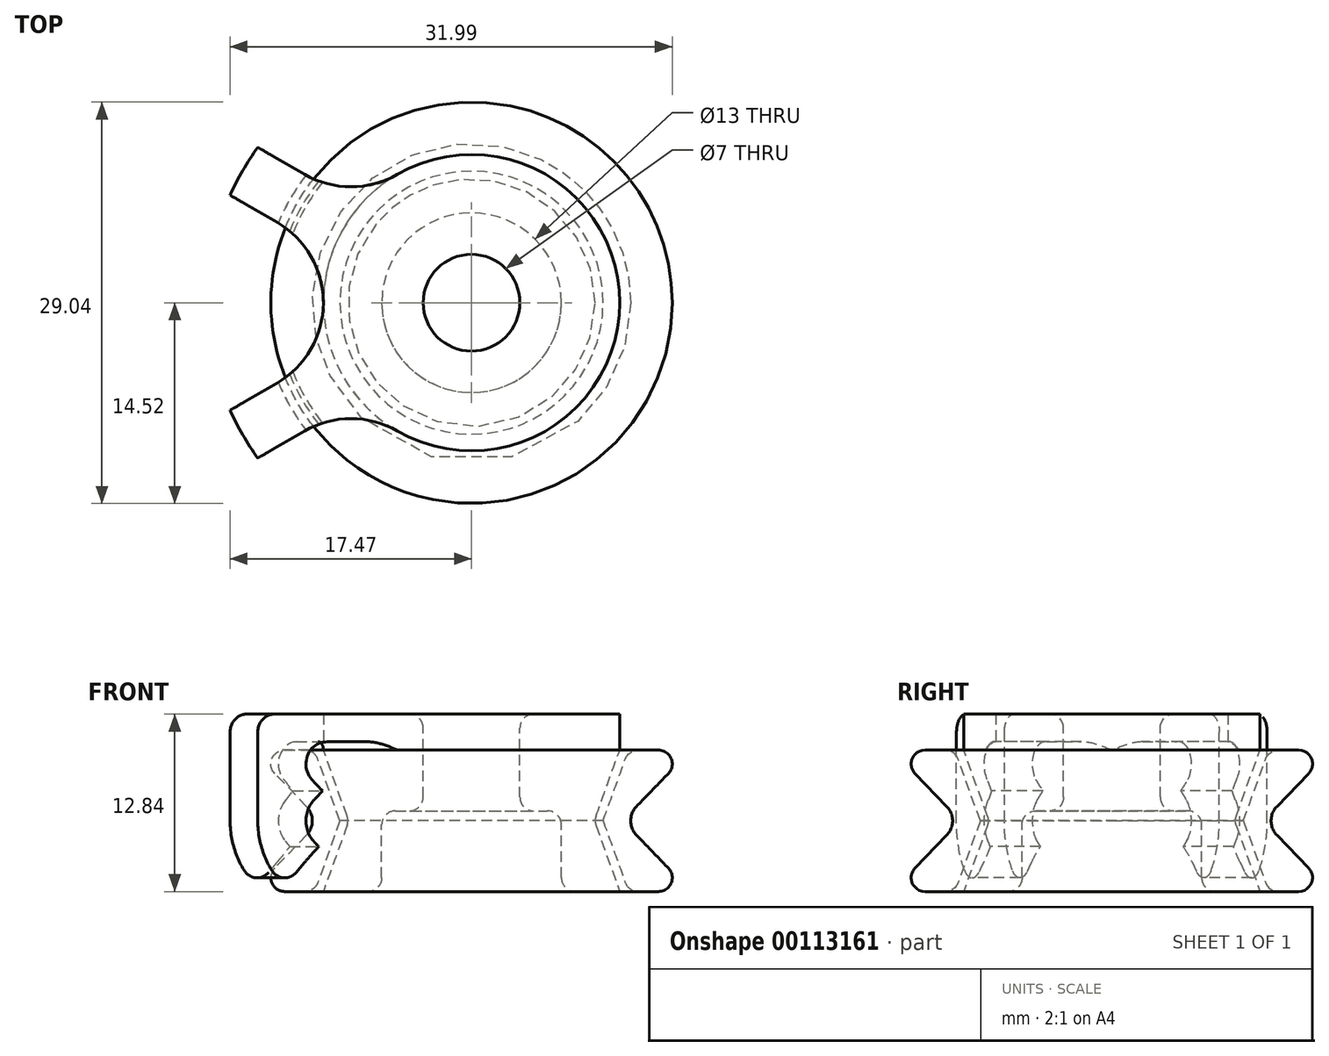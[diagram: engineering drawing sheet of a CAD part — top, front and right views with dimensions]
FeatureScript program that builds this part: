
annotation { "Feature Type Name" : "Feature", "Feature Type Description" : "" }
export const myFeature = defineFeature(function(context is Context, id is Id, definition is map)
    precondition{}
    {
        {
            assignVariable(context, id + "F0", {"name" : "WALL", "anyValue" : 4});
        }
        {
            assignVariable(context, id + "F1", {"name" : "ArmAngle", "anyValue" : 60});
        }
        {
            assignVariable(context, id + "F2", {"name" : "NumberArms", "anyValue" : 2});
        }
        {
            var Q0;
            Q0=qCreatedBy(makeId("Front.planeOp"),FACE);
            var sketch = newSketch(context, id + "F3", { "sketchPlane" : qUnion([Q0])});
            skLineSegment(sketch, "E0", {"start": v(0, 5.12) * mm, "end": v(0, -5.12) * mm});
            skLineSegment(sketch, "E1", {"start": v(-11.36, -5.12) * mm, "end": v(-13.52, -5.12) * mm});
            skLineSegment(sketch, "E2", {"start": v(-13.52, 5.12) * mm, "end": v(-11.36, 5.12) * mm});
            skCircle(sketch, "E3", {"center": v(-13.02, 0) * mm, "radius": 1.5 * mm, "construction": true});
            skLineSegment(sketch, "E4", {"start": v(-11.94, 1.04) * mm, "end": v(-14.24, 3.42) * mm});
            skLineSegment(sketch, "E5", {"start": v(-14.24, -3.42) * mm, "end": v(-11.94, -1.04) * mm});
            skArc(sketch, "E6", {"start": v(-11.94, -1.04) * mm, "mid": v(-11.52, 0) * mm, "end": v(-11.94, 1.04) * mm});
            skLineSegment(sketch, "E7", {"start": v(-11.36, 5.12) * mm, "end": v(-9.52, 0) * mm});
            skLineSegment(sketch, "E8", {"start": v(-9.52, 0) * mm, "end": v(-11.36, -5.12) * mm});
            skLineSegment(sketch, "E9", {"start": v(-10.72, 5.12) * mm, "end": v(-8.88, 0) * mm});
            skLineSegment(sketch, "E10", {"start": v(-8.88, 0) * mm, "end": v(-10.72, -5.12) * mm});
            skLineSegment(sketch, "E11", {"start": v(-10.72, 5.12) * mm, "end": v(-6.5, 5.12) * mm});
            skLineSegment(sketch, "E12", {"start": v(-6.5, 5.12) * mm, "end": v(-6.5, -5.12) * mm});
            skLineSegment(sketch, "E13", {"start": v(-6.5, -5.12) * mm, "end": v(-10.72, -5.12) * mm});
            skArc(sketch, "E14", {"start": v(-14.53, 1.46) * mm, "mid": v(-15.12, 0) * mm, "end": v(-14.53, -1.46) * mm});
            skLineSegment(sketch, "E15", {"start": v(-10.72, 5.12) * mm, "end": v(-10.72, 5.12) * mm});
            skLineSegment(sketch, "E16", {"start": v(-11.32, 5.72) * mm, "end": v(-13.52, 5.72) * mm});
            skLineSegment(sketch, "E17", {"start": v(-6.5, 5.12) * mm, "end": v(-6.5, 7.72) * mm});
            skLineSegment(sketch, "E18", {"start": v(-6.5, 7.72) * mm, "end": v(-19.12, 7.72) * mm});
            skLineSegment(sketch, "E19", {"start": v(-16.88, -4.72) * mm, "end": v(-14.13, -1.87) * mm});
            skLineSegment(sketch, "E20", {"start": v(-14.53, 1.46) * mm, "end": v(-13.85, 2.16) * mm});
            skLineSegment(sketch, "E21", {"start": v(-14.53, -1.46) * mm, "end": v(-14.13, -1.87) * mm});
            skPoint(sketch, "E22.visualSharp", {"position": v(-15.88, 5.12) * mm});
            skArc(sketch, "E22.filletArc", {"start": v(-13.52, 5.12) * mm, "mid": v(-14.44, 4.5) * mm, "end": v(-14.24, 3.42) * mm});
            skPoint(sketch, "E23.visualSharp", {"position": v(-15.88, -5.12) * mm});
            skArc(sketch, "E23.filletArc", {"start": v(-14.24, -3.42) * mm, "mid": v(-14.44, -4.5) * mm, "end": v(-13.52, -5.12) * mm});
            skLineSegment(sketch, "E24", {"start": v(-13.02, 0) * mm, "end": v(-13.02, 8.16) * mm, "construction": true});
            skArc(sketch, "E25", {"start": v(-13.52, 5.72) * mm, "mid": v(-15, 4.74) * mm, "end": v(-14.67, 3) * mm});
            skArc(sketch, "E26", {"start": v(-19.12, 0) * mm, "mid": v(-18.53, -2.61) * mm, "end": v(-16.88, -4.72) * mm});
            skLineSegment(sketch, "E27", {"start": v(-19.12, 0) * mm, "end": v(-19.12, 7.72) * mm});
            skLineSegment(sketch, "E28", {"start": v(-10.72, 5.72) * mm, "end": v(-10.72, 7.72) * mm});
            skLineSegment(sketch, "E29", {"start": v(-13.52, 5.72) * mm, "end": v(-13.52, 7.72) * mm});
            skPoint(sketch, "E30.visualSharp", {"position": v(-10.72, 5.72) * mm});
            skArc(sketch, "E30.filletArc", {"start": v(-10.72, 5.12) * mm, "mid": v(-10.9, 5.54) * mm, "end": v(-11.32, 5.72) * mm});
            skLineSegment(sketch, "E31", {"start": v(-16.34, -5.12) * mm, "end": v(-17.27, -5.12) * mm});
            skLineSegment(sketch, "E32", {"start": v(-6.5, 0.72) * mm, "end": v(-3.5, 0.72) * mm});
            skLineSegment(sketch, "E33", {"start": v(-3.5, 0.72) * mm, "end": v(-3.5, 5.12) * mm});
            skLineSegment(sketch, "E34", {"start": v(-3.5, 5.12) * mm, "end": v(-6.5, 5.12) * mm});
            skLineSegment(sketch, "E35", {"start": v(-3.5, 5.12) * mm, "end": v(-3.5, 7.72) * mm});
            skLineSegment(sketch, "E36", {"start": v(-3.5, 7.72) * mm, "end": v(-6.5, 7.72) * mm});
            skLineSegment(sketch, "E37", {"start": v(-14.52, 0) * mm, "end": v(-14.52, 8.2) * mm, "construction": true});
            skLineSegment(sketch, "E38", {"start": v(-14.67, 3) * mm, "end": v(-13.85, 2.16) * mm});
            skSolve(sketch);
        }
        {
            var Q0;
            Q0=makeQuery(id+"F3.imprint","IMPRINT",FACE,{"disambiguationData":[TD([[makeQuery(id+"F3.imprint","IMPRINT",EDGE,{"derivedFrom":sQuery(id+"F3.wireOp",EDGE,"E11")}),1.0]])]});
            var Q1;
            Q1=makeQuery(id+"F3.imprint","IMPRINT",FACE,{"disambiguationData":[TD([[makeQuery(id+"F3.imprint","IMPRINT",EDGE,{"derivedFrom":sQuery(id+"F3.wireOp",EDGE,"E16")}),-1.0]])]});
            var Q2;
            Q2=makeQuery(id+"F3.imprint","IMPRINT",FACE,{"disambiguationData":[TD([[makeQuery(id+"F3.imprint","IMPRINT",EDGE,{"derivedFrom":sQuery(id+"F3.wireOp",EDGE,"E14")}),-1.0]])]});
            var Q3;
            Q3=makeQuery(id+"F3.imprint","IMPRINT",FACE,{"disambiguationData":[TD([[makeQuery(id+"F3.imprint","IMPRINT",EDGE,{"derivedFrom":sQuery(id+"F3.wireOp",EDGE,"E17")}),-1.0]])]});
            var Q4;
            Q4=sQuery(id+"F3.wireOp",EDGE,"E0");
            revolve(context, id + "F4", {"entities" : qUnion([Q0, Q1, Q2, Q3]), "axis" : qUnion([Q4]), "revolveType" : RevolveType.FULL});
        }
        {
            var Q0;
            Q0=qCreatedBy(makeId("Top.planeOp"),FACE);
            var sketch = newSketch(context, id + "F5", { "sketchPlane" : qUnion([Q0])});
            skCircle(sketch, "E39", {"center": v(0, 0) * mm, "radius": 10.72 * mm});
            skLineSegment(sketch, "E40", {"start": v(0, 0) * mm, "end": v(-17.37, 10.03) * mm, "construction": true});
            skLineSegment(sketch, "E41", {"start": v(-8.12, 7) * mm, "end": v(-25.94, 17.28) * mm});
            skLineSegment(sketch, "E42", {"start": v(-10.12, 3.53) * mm, "end": v(-27.94, 13.82) * mm});
            skLineSegment(sketch, "E43", {"start": v(-25.94, 17.28) * mm, "end": v(-27.94, 13.82) * mm});
            skCircle(sketch, "E44", {"center": v(-17.44, 0) * mm, "radius": 6.72 * mm});
            skCircle(sketch, "E45", {"center": v(-8.72, 15.1) * mm, "radius": 6.72 * mm});
            skLineSegment(sketch, "E46.MirrorCS", {"start": v(-10.12, -3.53) * mm, "end": v(-27.94, -13.82) * mm});
            skLineSegment(sketch, "E47.MirrorCS", {"start": v(-8.12, -7) * mm, "end": v(-25.94, -17.28) * mm});
            skLineSegment(sketch, "E48.MirrorCS", {"start": v(-25.94, -17.28) * mm, "end": v(-27.94, -13.82) * mm});
            skLineSegment(sketch, "E49.MirrorCS", {"start": v(0, 0) * mm, "end": v(-17.37, -10.03) * mm, "construction": true});
            skCircle(sketch, "E50.MirrorC", {"center": v(-8.72, -15.1) * mm, "radius": 6.72 * mm});
            skSolve(sketch);
        }
        {
            var Q0;
            {var subQ0=sQuery(id+"F5.wireOp",EDGE,"E39");var subQ4=makeQuery(id+"F5.imprint","INTERSECT",VERTEX,{"derivedFrom":[subQ0,sQuery(id+"F5.wireOp",EDGE,"E41")]});Q0=makeQuery(id+"F5.imprint","IMPRINT",FACE,{"disambiguationData":[TD([[makeQuery(id+"F5.imprint","IMPRINT",EDGE,{"disambiguationData":[TD([[subQ4,1.0]])],"derivedFrom":subQ0}),1.0]])]});}
            var Q1;
            {var subQ4=sQuery(id+"F5.wireOp",EDGE,"E48.MirrorCS");Q1=makeQuery(id+"F5.imprint","IMPRINT",FACE,{"disambiguationData":[TD([[makeQuery(id+"F5.imprint","IMPRINT",EDGE,{"derivedFrom":subQ4}),-1.0]])]});}
            var Q2;
            {var subQ0=sQuery(id+"F5.wireOp",EDGE,"E47.MirrorCS");var subQ1=sQuery(id+"F5.wireOp",EDGE,"E39");var subQ2=makeQuery(id+"F5.imprint","INTERSECT",VERTEX,{"derivedFrom":[subQ1,subQ0]});Q2=makeQuery(id+"F5.imprint","IMPRINT",FACE,{"disambiguationData":[TD([[makeQuery(id+"F5.imprint","IMPRINT",EDGE,{"disambiguationData":[TD([[subQ2,-1.0]])],"derivedFrom":subQ1}),-1.0]])]});}
            var Q3;
            {var subQ0=sQuery(id+"F5.wireOp",EDGE,"E46.MirrorCS");var subQ1=sQuery(id+"F5.wireOp",EDGE,"E39");var subQ2=makeQuery(id+"F5.imprint","INTERSECT",VERTEX,{"derivedFrom":[subQ1,subQ0]});Q3=makeQuery(id+"F5.imprint","IMPRINT",FACE,{"disambiguationData":[TD([[makeQuery(id+"F5.imprint","IMPRINT",EDGE,{"disambiguationData":[TD([[subQ2,1.0]])],"derivedFrom":subQ1}),-1.0]])]});}
            var Q4;
            Q4=makeQuery(id+"F4.opRevolve","SWEPT_FACE",FACE,{"disambiguationData":[OSD([sQuery(id+"F3.wireOp",EDGE,"E18")])]});
            extrude(context, id + "F6", {"entities" : qUnion([Q0, Q1, Q2, Q3]), "operationType" : NewBodyOperationType.INTERSECT, "endBound" : BoundingType.THROUGH_ALL, "endBoundEntityFace" : qUnion([Q4]), "depth" : 25 * mm, "hasSecondDirection" : true, "secondDirectionBound" : SecondDirectionBoundingType.THROUGH_ALL, "secondDirectionOppositeDirection" : true, "secondDirectionDepth" : 25 * mm});
        }
        {
            var Q0;
            Q0=makeQuery(id+"F6.boolean.opBoolean","INTERSECT",EDGE,{"derivedFrom":[makeQuery(id+"F4.opRevolve","SWEPT_FACE",FACE,{"disambiguationData":[OSD([sQuery(id+"F3.wireOp",EDGE,"E14")])]}),makeQuery(id+"F6.boolean.toolComplement.opBoolean","COPY",FACE,{"derivedFrom":makeQuery(id+"F6.opExtrude","SWEPT_FACE",FACE,{"disambiguationData":[OSD([sQuery(id+"F5.wireOp",EDGE,"E50.MirrorC")])]})})]});
            var Q1;
            Q1=makeQuery(id+"F6.boolean.opBoolean","INTERSECT",EDGE,{"derivedFrom":[makeQuery(id+"F4.opRevolve","SWEPT_FACE",FACE,{"disambiguationData":[OSD([sQuery(id+"F3.wireOp",EDGE,"E14")])]}),makeQuery(id+"F6.boolean.toolComplement.opBoolean","COPY",FACE,{"derivedFrom":makeQuery(id+"F6.opExtrude","SWEPT_FACE",FACE,{"disambiguationData":[OSD([sQuery(id+"F5.wireOp",EDGE,"E44")])]})})]});
            var Q2;
            Q2=makeQuery(id+"F6.boolean.opBoolean","INTERSECT",EDGE,{"derivedFrom":[makeQuery(id+"F4.opRevolve","SWEPT_FACE",FACE,{"disambiguationData":[OSD([sQuery(id+"F3.wireOp",EDGE,"E25")])]}),makeQuery(id+"F6.boolean.toolComplement.opBoolean","COPY",FACE,{"derivedFrom":makeQuery(id+"F6.opExtrude","SWEPT_FACE",FACE,{"disambiguationData":[OSD([sQuery(id+"F5.wireOp",EDGE,"E50.MirrorC")])]})})]});
            var Q3;
            Q3=makeQuery(id+"F6.boolean.opBoolean","INTERSECT",EDGE,{"derivedFrom":[makeQuery(id+"F4.opRevolve","SWEPT_FACE",FACE,{"disambiguationData":[OSD([sQuery(id+"F3.wireOp",EDGE,"E25")])]}),makeQuery(id+"F6.boolean.toolComplement.opBoolean","COPY",FACE,{"derivedFrom":makeQuery(id+"F6.opExtrude","SWEPT_FACE",FACE,{"disambiguationData":[OSD([sQuery(id+"F5.wireOp",EDGE,"E44")])]})})]});
            var Q4;
            Q4=makeQuery(id+"F4.opRevolve","SWEPT_EDGE",EDGE,{"disambiguationData":[OSD([sQuery(id+"F3.wireOp",EDGE,"E18"),sQuery(id+"F3.wireOp",EDGE,"E27")])]});
            var Q5;
            Q5=makeQuery(id+"F6.boolean.opBoolean","INTERSECT",EDGE,{"derivedFrom":[makeQuery(id+"F4.opRevolve","SWEPT_FACE",FACE,{"disambiguationData":[OSD([sQuery(id+"F3.wireOp",EDGE,"E27")])]}),makeQuery(id+"F6.boolean.toolComplement.opBoolean","COPY",FACE,{"derivedFrom":makeQuery(id+"F6.opExtrude","SWEPT_FACE",FACE,{"disambiguationData":[OSD([sQuery(id+"F5.wireOp",EDGE,"E47.MirrorCS")])]})})]});
            var Q6;
            Q6=makeQuery(id+"F4.opRevolve","SWEPT_EDGE",EDGE,{"disambiguationData":[OSD([sQuery(id+"F3.wireOp",EDGE,"E19"),sQuery(id+"F3.wireOp",EDGE,"E26")])]});
            fillet(context, id + "F7", {"entities" : qUnion([Q0, Q1, Q2, Q3, Q4, Q5, Q6]), "radius" : (getVariable(context, 'WALL') / 3) * mm, "tangentPropagation" : true, "allowEdgeOverflow" : false});
        }
        {
            var Q0;
            Q0=makeQuery(id+"F3.imprint","IMPRINT",FACE,{"disambiguationData":[TD([[makeQuery(id+"F3.imprint","IMPRINT",EDGE,{"derivedFrom":sQuery(id+"F3.wireOp",EDGE,"E9")}),1.0]])]});
            var Q1;
            Q1=makeQuery(id+"F3.imprint","IMPRINT",FACE,{"disambiguationData":[TD([[makeQuery(id+"F3.imprint","IMPRINT",EDGE,{"derivedFrom":sQuery(id+"F3.wireOp",EDGE,"E1")}),-1.0]])]});
            var Q2;
            {var subQ2=sQuery(id+"F3.wireOp",EDGE,"E32");Q2=makeQuery(id+"F3.imprint","IMPRINT",FACE,{"disambiguationData":[TD([[makeQuery(id+"F3.imprint","IMPRINT",EDGE,{"derivedFrom":subQ2}),1.0]])]});}
            var Q3;
            Q3=sQuery(id+"F3.wireOp",EDGE,"E0");
            revolve(context, id + "F8", {"entities" : qUnion([Q0, Q1, Q2]), "axis" : qUnion([Q3]), "revolveType" : RevolveType.FULL});
        }
        {
            var Q0;
            Q0=makeQuery(id+"F4.opRevolve","SWEPT_BODY",BODY,{"disambiguationData":[OSD([sQuery(id+"F3.wireOp",EDGE,"E11"),sQuery(id+"F3.wireOp",EDGE,"E14"),sQuery(id+"F3.wireOp",EDGE,"E16"),sQuery(id+"F3.wireOp",EDGE,"E18"),sQuery(id+"F3.wireOp",EDGE,"E19"),sQuery(id+"F3.wireOp",EDGE,"E20"),sQuery(id+"F3.wireOp",EDGE,"E21"),sQuery(id+"F3.wireOp",EDGE,"E25"),sQuery(id+"F3.wireOp",EDGE,"E26"),sQuery(id+"F3.wireOp",EDGE,"E27"),sQuery(id+"F3.wireOp",EDGE,"E30.filletArc"),sQuery(id+"F3.wireOp",EDGE,"E31"),sQuery(id+"F3.wireOp",EDGE,"E34"),sQuery(id+"F3.wireOp",EDGE,"E35"),sQuery(id+"F3.wireOp",EDGE,"E36")])]});
            var Q1;
            Q1=sQuery(id+"F3.wireOp",EDGE,"E0");
            circularPattern(context, id + "F9", {"operationType" : NewBodyOperationType.ADD, "entities" : qUnion([Q0]), "axis" : qUnion([Q1]), "angle" : (getVariable(context, 'ArmAngle')) * degree, "instanceCount" : getVariable(context, 'NumberArms')});
        }
        {
            var Q0;
            Q0=makeQuery(id+"F8.opRevolve","SWEPT_EDGE",EDGE,{"disambiguationData":[OSD([sQuery(id+"F3.wireOp",EDGE,"E1"),sQuery(id+"F3.wireOp",EDGE,"E8")])]});
            var Q1;
            Q1=makeQuery(id+"F8.opRevolve","SWEPT_EDGE",EDGE,{"disambiguationData":[OSD([sQuery(id+"F3.wireOp",EDGE,"E2"),sQuery(id+"F3.wireOp",EDGE,"E7")])]});
            var Q2;
            Q2=makeQuery(id+"F8.opRevolve","SWEPT_EDGE",EDGE,{"disambiguationData":[OSD([sQuery(id+"F3.wireOp",EDGE,"E9"),sQuery(id+"F3.wireOp",EDGE,"E10")])]});
            var Q3;
            Q3=makeQuery(id+"F8.opRevolve","SWEPT_FACE",FACE,{"disambiguationData":[OSD([sQuery(id+"F3.wireOp",EDGE,"E33")])]});
            var Q4;
            Q4=makeQuery(id+"F4.opRevolve","SWEPT_FACE",FACE,{"disambiguationData":[OSD([sQuery(id+"F3.wireOp",EDGE,"E35")])]});
            var Q5;
            Q5=makeQuery(id+"F8.opRevolve","SWEPT_EDGE",EDGE,{"disambiguationData":[OSD([sQuery(id+"F3.wireOp",EDGE,"E12"),sQuery(id+"F3.wireOp",EDGE,"E32")])]});
            var Q6;
            Q6=makeQuery(id+"F8.opRevolve","SWEPT_EDGE",EDGE,{"disambiguationData":[OSD([sQuery(id+"F3.wireOp",EDGE,"E12"),sQuery(id+"F3.wireOp",EDGE,"E13")])]});
            fillet(context, id + "F10", {"entities" : qUnion([Q0, Q1, Q2, Q3, Q4, Q5, Q6]), "radius" : 1 * mm, "tangentPropagation" : true, "allowEdgeOverflow" : false});
        }
    });
